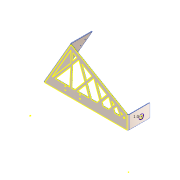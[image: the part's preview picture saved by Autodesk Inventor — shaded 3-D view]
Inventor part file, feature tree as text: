
AUTODESK INVENTOR PART (.ipt)
format: ipt  version: 2016 (Build 200138000, 138)  size: 424,448 bytes
history: native  units: in
note: dims shown in document units (in); Inventor stores cm internally (conversion verified against a paired STEP export)
features: reference x15, sketch x11, sheet_metal_op x9, other x8, projected_geometry x3, hole x2, fillet x1
ambient origin geometry x8: Origin, YZ Plane, XZ Plane, XY Plane, X Axis, Y Axis, Z Axis, Center Point
bodies: Solid1 (feature_tree)
feature tree (49):
  sheet_metal_op  "Face1"
  sheet_metal_op  "Flange1"
  sketch  "Sketch5"  dims[d10=90.0deg]
  sheet_metal_op  "Flange2"
  fillet  "Fillet1"  Radius=30.0in
  sketch  "Sketch7"  dims[d12=0.125in]
  hole  "Hole1"  [1 undecoded]
  hole  "Hole2"  [1 undecoded]
  sketch  "Sketch11"  dims[d16=0.25in]
  sheet_metal_op  "Face2"
  sketch  "Sketch1"  dims[d1=30.0in d2=0.125in]
  other  "Plate1"
  sketch  "Sketch3"  dims[d7=60.0deg d8=3.0in]
  reference  "Reference12"
  reference  "Reference13"
  reference  "Reference14"
  sketch  "Sketch4"  dims[d9=180.0deg]
  other  "Plate2"
  sheet_metal_op  "Bend1"
  sheet_metal_op  "Corner1"
  reference  "Reference15"
  reference  "Reference16"
  reference  "Reference17"
  sketch  "Sketch6"  dims[d11=13.0167in]
  other  "Plate3"
  sheet_metal_op  "Bend2"
  sheet_metal_op  "Corner2"
  reference  "Reference18"
  reference  "Reference19"
  reference  "Reference20"
  reference  "Reference21"
  reference  "Reference22"
  sketch  "Sketch8"  dims[d13=0.0in]
  reference  "Reference23"
  reference  "Reference24"
  reference  "Reference25"
  reference  "Reference26"
  sketch  "Sketch9"  dims[d14=0.125in]
  projected_geometry  "Projected Loop1"
  sketch  "Sketch10"  dims[d15=0.0625in]
  projected_geometry  "Projected Loop2"
  projected_geometry  "Projected Loop3"
  sketch  "Sketch12"  dims[d17=0.125in d18=5.0in d19=90.0deg d20=0.125in d21=0.5in d22=0.125in d23=0.125in d24=0.125in d25=0.0625in d26=0.25in d27=0.125in d28=5.0in d29=90.0deg d30=0.125in d31=0.5in d32=0.125in d33=0.125in d36=1.063in d37=0.125in d38=0.0in d39=0.125in d40=0.19in d41=0.75in d42=0.375in d43=0.25in d44=0.5635in d45=0.125in d46=0.8108in d47=2.0in d48=2.0in d50=2.0in d51=2.0in d53=0.19in d54=0.75in d55=0.375in d56=0.25in d57=0.5635in d58=0.125in d59=0.8108in d60=0.5in d61=90.0deg d63=0.5in d64=0.5in d65=0.5in d79=0.25in d80=0.25in d95=180.0deg d96=0.5in d98=1.5in d99=0.125in d100=0.0in d101=0.125in d102=0.125in d103=0.0625in d104=0.25in d105=0.125in]
  other  "Plate4"
  sheet_metal_op  "Bend3"
  other  "Cut1"
  other  "Cut2"
  other  "Cut3"
  other  "Definition1"
note: 2 required parameter values undecoded (feature->parameter linkage not recoverable at this tier; creation-order binding heuristic only, values carry confidence <= 0.55)
